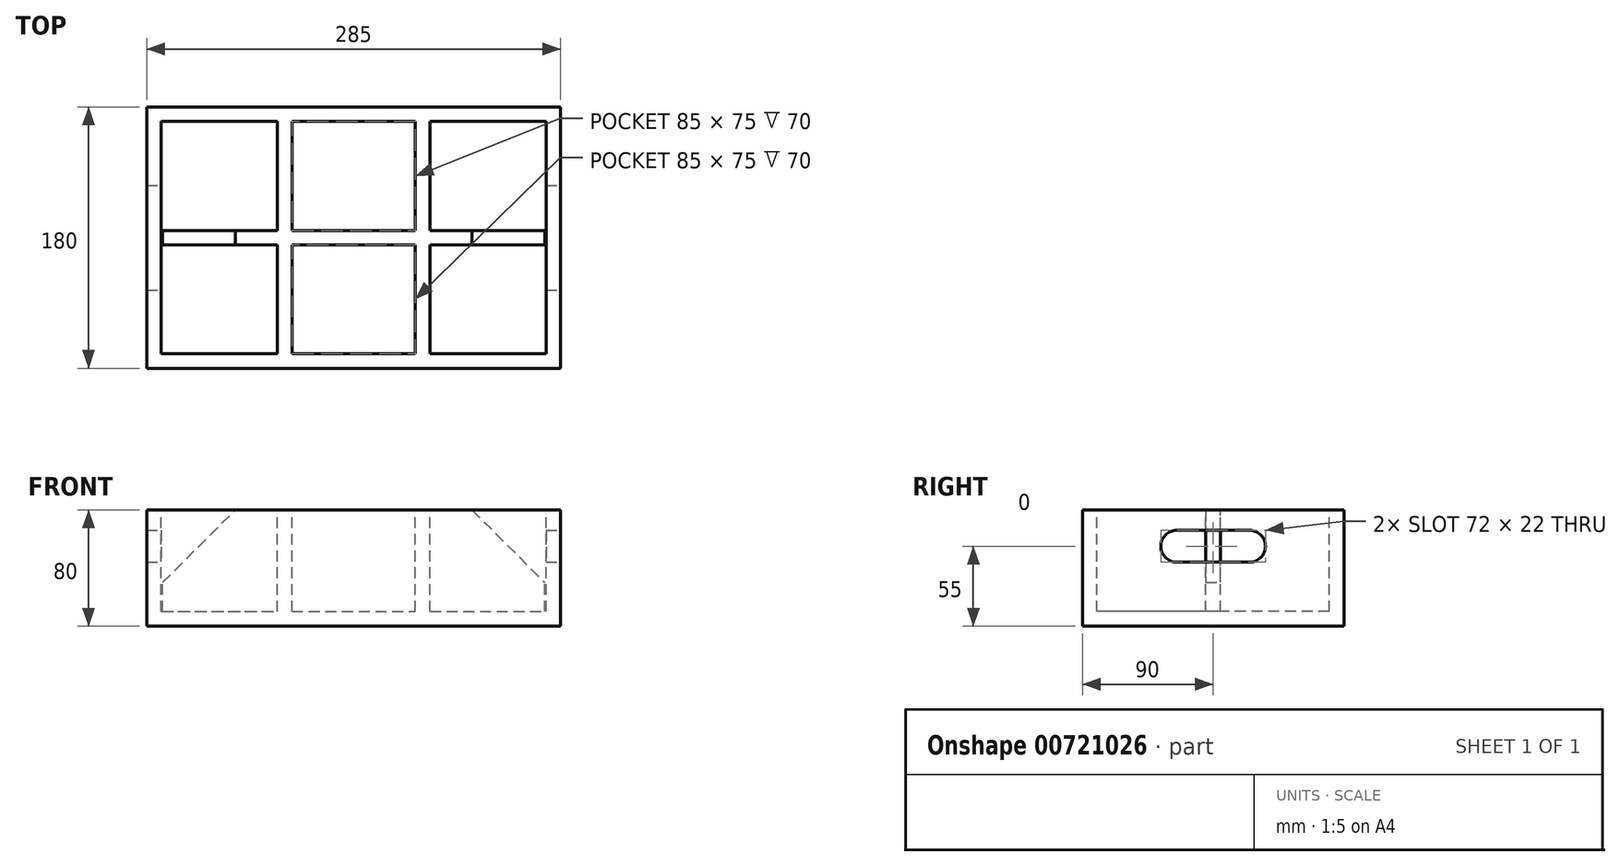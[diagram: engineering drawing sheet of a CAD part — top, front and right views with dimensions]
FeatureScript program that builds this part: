
annotation { "Feature Type Name" : "Feature", "Feature Type Description" : "" }
export const myFeature = defineFeature(function(context is Context, id is Id, definition is map)
    precondition{}
    {
        {
            var Q0;
            Q0=qCreatedBy(makeId("Front.planeOp"),FACE);
            var sketch = newSketch(context, id + "F0", { "sketchPlane" : qUnion([Q0])});
            skLineSegment(sketch, "E0.bottom", {"start": v(0, 0) * mm, "end": v(285, 0) * mm});
            skLineSegment(sketch, "E0.top", {"start": v(0, 80) * mm, "end": v(285, 80) * mm});
            skLineSegment(sketch, "E0.left", {"start": v(0, 0) * mm, "end": v(0, 80) * mm});
            skLineSegment(sketch, "E0.right", {"start": v(285, 0) * mm, "end": v(285, 80) * mm});
            skSolve(sketch);
        }
        {
            var Q0;
            Q0=makeQuery(id+"F0.imprint","IMPRINT",FACE,{"disambiguationData":[TD([[makeQuery(id+"F0.imprint","IMPRINT",EDGE,{"derivedFrom":sQuery(id+"F0.wireOp",EDGE,"E0.bottom")}),1.0]])]});
            extrude(context, id + "F1", {"entities" : qUnion([Q0]), "oppositeDirection" : true, "depth" : 180 * mm, "offsetDistance" : 25 * mm});
        }
        {
            var Q0;
            Q0=makeQuery(id+"F1.opExtrude","SWEPT_FACE",FACE,{"disambiguationData":[OSD([sQuery(id+"F0.wireOp",EDGE,"E0.top")])]});
            var sketch = newSketch(context, id + "F2", { "sketchPlane" : qUnion([Q0])});
            skLineSegment(sketch, "E1.0", {"start": v(10, 170) * mm, "end": v(275, 170) * mm});
            skLineSegment(sketch, "E2.0", {"start": v(10, 170) * mm, "end": v(10, 10) * mm});
            skLineSegment(sketch, "E3.0", {"start": v(10, 10) * mm, "end": v(275, 10) * mm});
            skLineSegment(sketch, "E4.0", {"start": v(275, 170) * mm, "end": v(275, 10) * mm});
            skSolve(sketch);
        }
        {
            var Q0;
            Q0=qSketchRegion(id+"F2",true);
            extrude(context, id + "F3", {"entities" : qUnion([Q0]), "operationType" : NewBodyOperationType.REMOVE, "oppositeDirection" : true, "depth" : 70 * mm, "offsetDistance" : 25 * mm});
        }
        {
            var Q0;
            Q0=makeQuery(id+"F1.opExtrude","SWEPT_FACE",FACE,{"disambiguationData":[OSD([sQuery(id+"F0.wireOp",EDGE,"E0.right")])]});
            var sketch = newSketch(context, id + "F4", { "sketchPlane" : qUnion([Q0])});
            skArc(sketch, "E5", {"start": v(65, 66) * mm, "mid": v(54, 55) * mm, "end": v(65, 44) * mm});
            skArc(sketch, "E6", {"start": v(115, 44) * mm, "mid": v(126, 55) * mm, "end": v(115, 66) * mm});
            skPoint(sketch, "E7", {"position": v(90, 75) * mm});
            skLineSegment(sketch, "E8", {"start": v(65, 66) * mm, "end": v(115, 66) * mm});
            skLineSegment(sketch, "E9", {"start": v(115, 44) * mm, "end": v(65, 44) * mm});
            skPoint(sketch, "E10", {"position": v(0, 80) * mm});
            skPoint(sketch, "E11", {"position": v(180, 80) * mm});
            skSolve(sketch);
        }
        {
            var Q0;
            Q0=makeQuery(id+"F4.imprint","IMPRINT",FACE,{"disambiguationData":[TD([[makeQuery(id+"F4.imprint","IMPRINT",EDGE,{"derivedFrom":sQuery(id+"F4.wireOp",EDGE,"E5")}),1.0]])]});
            extrude(context, id + "F5", {"entities" : qUnion([Q0]), "operationType" : NewBodyOperationType.REMOVE, "endBound" : BoundingType.THROUGH_ALL, "oppositeDirection" : true, "depth" : 25 * mm, "offsetDistance" : 25 * mm});
        }
        {
            var Q0;
            Q0=makeQuery(id+"F1.opExtrude","SWEPT_FACE",FACE,{"disambiguationData":[OSD([sQuery(id+"F0.wireOp",EDGE,"E0.top")])]});
            var sketch = newSketch(context, id + "F6", { "sketchPlane" : qUnion([Q0])});
            skLineSegment(sketch, "E12", {"start": v(90, 170) * mm, "end": v(90, 95) * mm});
            skLineSegment(sketch, "E13", {"start": v(195, 170) * mm, "end": v(195, 95) * mm});
            skLineSegment(sketch, "E14.0", {"start": v(100, 170) * mm, "end": v(100, 95) * mm});
            skLineSegment(sketch, "E15.0", {"start": v(185, 170) * mm, "end": v(185, 95) * mm});
            skLineSegment(sketch, "E16", {"start": v(11, 95) * mm, "end": v(90, 95) * mm});
            skLineSegment(sketch, "E17.0", {"start": v(11, 85) * mm, "end": v(90, 85) * mm});
            skLineSegment(sketch, "E18.trimOffspring", {"start": v(90, 85) * mm, "end": v(90, 10) * mm});
            skLineSegment(sketch, "E19.trimOffspring", {"start": v(100, 95) * mm, "end": v(185, 95) * mm});
            skLineSegment(sketch, "E20.trimOffspring", {"start": v(100, 85) * mm, "end": v(100, 10) * mm});
            skLineSegment(sketch, "E21.trimOffspring", {"start": v(100, 85) * mm, "end": v(185, 85) * mm});
            skLineSegment(sketch, "E22.trimOffspring", {"start": v(185, 85) * mm, "end": v(185, 10) * mm});
            skLineSegment(sketch, "E23.trimOffspring", {"start": v(195, 85) * mm, "end": v(195, 10) * mm});
            skLineSegment(sketch, "E24.trimOffspring", {"start": v(195, 85) * mm, "end": v(274, 85) * mm});
            skLineSegment(sketch, "E25.trimOffspring", {"start": v(195, 95) * mm, "end": v(274, 95) * mm});
            skLineSegment(sketch, "E26", {"start": v(90, 170) * mm, "end": v(100, 170) * mm});
            skLineSegment(sketch, "E27", {"start": v(185, 170) * mm, "end": v(195, 170) * mm});
            skLineSegment(sketch, "E28", {"start": v(195, 10) * mm, "end": v(185, 10) * mm});
            skLineSegment(sketch, "E29", {"start": v(100, 10) * mm, "end": v(90, 10) * mm});
            skLineSegment(sketch, "E30.0", {"start": v(11, 95) * mm, "end": v(11, 85) * mm});
            skLineSegment(sketch, "E31.0", {"start": v(274, 95) * mm, "end": v(274, 85) * mm});
            skSolve(sketch);
        }
        {
            var Q0;
            Q0=makeQuery(id+"F6.imprint","IMPRINT",FACE,{"disambiguationData":[TD([[makeQuery(id+"F6.imprint","IMPRINT",EDGE,{"derivedFrom":sQuery(id+"F6.wireOp",EDGE,"E12")}),1.0]])]});
            extrude(context, id + "F7", {"entities" : qUnion([Q0]), "operationType" : NewBodyOperationType.ADD, "oppositeDirection" : true, "depth" : 70 * mm, "offsetDistance" : 25 * mm});
        }
        {
            var Q0;
            Q0=makeQuery(id+"F7.opExtrude","CAP_EDGE",EDGE,{"disambiguationData":[OSD([sQuery(id+"F6.wireOp",EDGE,"E30.0")])],"isStart":true});
            var Q1;
            Q1=makeQuery(id+"F7.opExtrude","CAP_EDGE",EDGE,{"disambiguationData":[OSD([sQuery(id+"F6.wireOp",EDGE,"E31.0")])],"isStart":true});
            chamfer(context, id + "F8", {"entities" : qUnion([Q0, Q1]), "chamferType" : ChamferType.OFFSET_ANGLE, "width" : 50 * mm, "oppositeDirection" : false, "angle" : 45 * degree, "tangentPropagation" : true});
        }
    });
